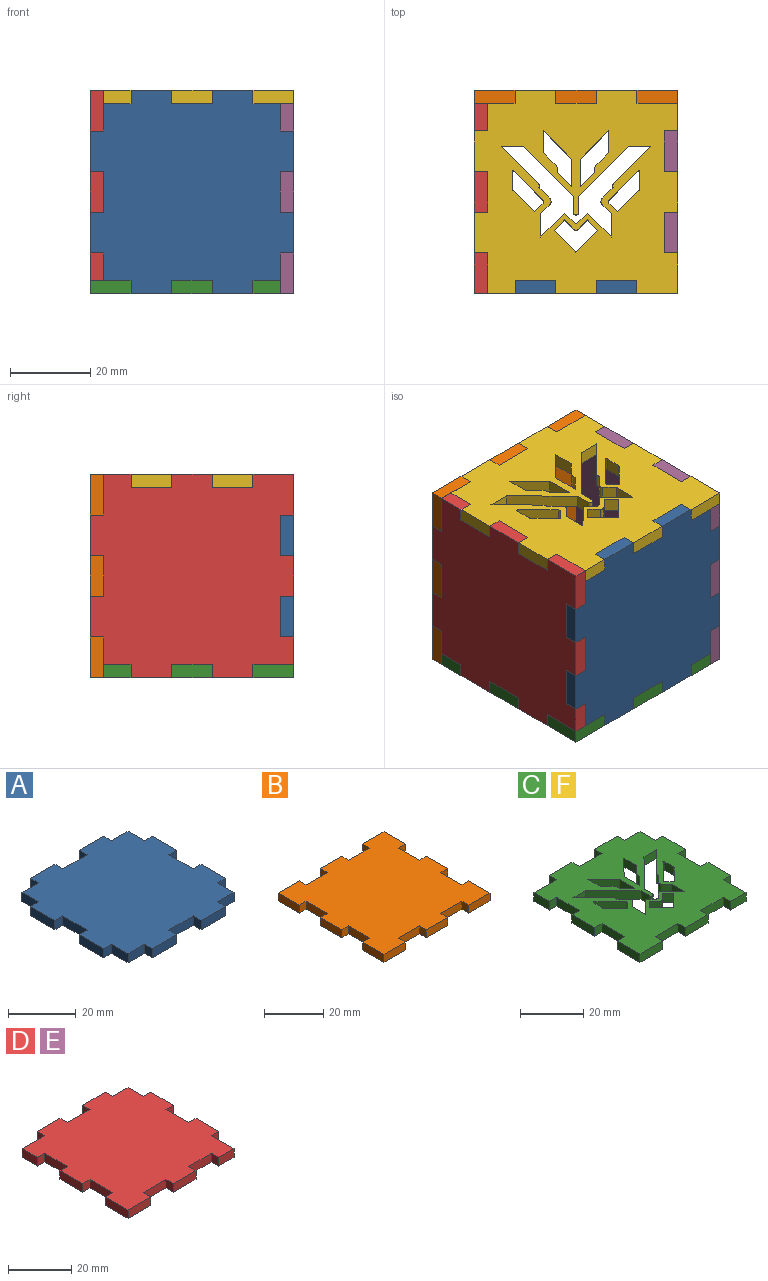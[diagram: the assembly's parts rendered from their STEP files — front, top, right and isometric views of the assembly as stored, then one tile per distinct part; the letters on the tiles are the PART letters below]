
ASSEMBLY  parts=6 mates=5
PART A: 38 faces, bbox 50.8x50.8x3.3 mm
  f0: plane 3.3x3.3mm, normal (-1,0,0), area 10.9mm2, adj f1,f35,f36,f37
  f1: plane 6.86x3.3mm, normal (0,1,0), area 22.6mm2, adj f0,f2,f36,f37
  f2: plane 6.86x3.3mm, normal (-1,0,0), area 22.6mm2, adj f1,f3,f36,f37
  f3: plane 3.3x3.3mm, normal (0,1,0), area 10.9mm2, adj f2,f4,f36,f37
  f4: plane 10.16x3.3mm, normal (-1,0,0), area 33.5mm2, adj f3,f5,f36,f37
  f5: plane 3.3x3.3mm, normal (0,-1,0), area 10.9mm2, adj f4,f6,f36,f37
  f6: plane 10.16x3.3mm, normal (-1,0,0), area 33.5mm2, adj f5,f7,f36,f37
  f7: plane 3.3x3.3mm, normal (0,1,0), area 10.9mm2, adj f6,f8,f36,f37
  f8: plane 10.16x3.3mm, normal (-1,0,0), area 33.5mm2, adj f7,f9,f36,f37
  f9: plane 3.3x3.3mm, normal (0,-1,0), area 10.9mm2, adj f8,f10,f36,f37
  f10: plane 6.86x3.3mm, normal (-1,0,0), area 22.6mm2, adj f9,f11,f36,f37
  f11: plane 6.86x3.3mm, normal (0,-1,0), area 22.6mm2, adj f10,f12,f36,f37
  f12: plane 3.3x3.3mm, normal (-1,0,0), area 10.9mm2, adj f11,f13,f36,f37
  f13: plane 10.16x3.3mm, normal (0,-1,0), area 33.5mm2, adj f12,f14,f36,f37
  f14: plane 3.3x3.3mm, normal (1,0,0), area 10.9mm2, adj f13,f15,f36,f37
  f15: plane 10.16x3.3mm, normal (0,-1,0), area 33.5mm2, adj f14,f16,f36,f37
  f16: plane 3.3x3.3mm, normal (-1,0,0), area 10.9mm2, adj f15,f17,f36,f37
  f17: plane 10.16x3.3mm, normal (0,-1,0), area 33.5mm2, adj f16,f18,f36,f37
  f18: plane 3.3x3.3mm, normal (1,0,0), area 10.9mm2, adj f17,f19,f36,f37
  f19: plane 6.86x3.3mm, normal (0,-1,0), area 22.6mm2, adj f18,f20,f36,f37
  f20: plane 6.86x3.3mm, normal (1,0,0), area 22.6mm2, adj f19,f21,f36,f37
  f21: plane 3.3x3.3mm, normal (0,-1,0), area 10.9mm2, adj f20,f22,f36,f37
  f22: plane 10.16x3.3mm, normal (1,0,0), area 33.5mm2, adj f21,f23,f36,f37
  f23: plane 3.3x3.3mm, normal (0,1,0), area 10.9mm2, adj f22,f24,f36,f37
  f24: plane 10.16x3.3mm, normal (1,0,0), area 33.5mm2, adj f23,f25,f36,f37
  f25: plane 3.3x3.3mm, normal (0,-1,0), area 10.9mm2, adj f24,f26,f36,f37
  f26: plane 10.16x3.3mm, normal (1,0,0), area 33.5mm2, adj f25,f27,f36,f37
  f27: plane 3.3x3.3mm, normal (0,1,0), area 10.9mm2, adj f26,f28,f36,f37
  f28: plane 6.86x3.3mm, normal (1,0,0), area 22.6mm2, adj f27,f29,f36,f37
  f29: plane 6.86x3.3mm, normal (0,1,0), area 22.6mm2, adj f28,f30,f36,f37
  f30: plane 3.3x3.3mm, normal (1,0,0), area 10.9mm2, adj f29,f31,f36,f37
  f31: plane 10.16x3.3mm, normal (0,1,0), area 33.5mm2, adj f30,f32,f36,f37
  f32: plane 3.3x3.3mm, normal (-1,0,0), area 10.9mm2, adj f31,f33,f36,f37
  f33: plane 10.16x3.3mm, normal (0,1,0), area 33.5mm2, adj f32,f34,f36,f37
  f34: plane 3.3x3.3mm, normal (1,0,0), area 10.9mm2, adj f33,f35,f36,f37
  f35: plane 10.16x3.3mm, normal (0,1,0), area 33.5mm2, adj f0,f34,f36,f37
  f36: plane 50.8x50.8mm, normal (0,0,1), area 2221.9mm2, adj f0,f1,f2,f3,f4,f5,f6,f7
  f37: plane 50.8x50.8mm, normal (0,0,-1), area 2221.9mm2, adj f0,f1,f2,f3,f4,f5,f6,f7
PART B: 38 faces, bbox 50.8x50.8x3.3 mm
  f0: plane 10.16x3.3mm, normal (0,1,0), area 33.5mm2, adj f1,f35,f36,f37
  f1: plane 10.16x3.3mm, normal (-1,0,0), area 33.5mm2, adj f0,f2,f36,f37
  f2: plane 3.3x3.3mm, normal (0,-1,0), area 10.9mm2, adj f1,f3,f36,f37
  f3: plane 10.16x3.3mm, normal (-1,0,0), area 33.5mm2, adj f2,f4,f36,f37
  f4: plane 3.3x3.3mm, normal (0,1,0), area 10.9mm2, adj f3,f5,f36,f37
  f5: plane 10.16x3.3mm, normal (-1,0,0), area 33.5mm2, adj f4,f6,f36,f37
  f6: plane 3.3x3.3mm, normal (0,-1,0), area 10.9mm2, adj f5,f7,f36,f37
  f7: plane 10.16x3.3mm, normal (-1,0,0), area 33.5mm2, adj f6,f8,f36,f37
  f8: plane 3.3x3.3mm, normal (0,1,0), area 10.9mm2, adj f7,f9,f36,f37
  f9: plane 10.16x3.3mm, normal (-1,0,0), area 33.5mm2, adj f8,f10,f36,f37
  f10: plane 10.16x3.3mm, normal (0,-1,0), area 33.5mm2, adj f9,f11,f36,f37
  f11: plane 3.3x3.3mm, normal (1,0,0), area 10.9mm2, adj f10,f12,f36,f37
  f12: plane 10.16x3.3mm, normal (0,-1,0), area 33.5mm2, adj f11,f13,f36,f37
  f13: plane 3.3x3.3mm, normal (-1,0,0), area 10.9mm2, adj f12,f14,f36,f37
  f14: plane 10.16x3.3mm, normal (0,-1,0), area 33.5mm2, adj f13,f15,f36,f37
  f15: plane 3.3x3.3mm, normal (1,0,0), area 10.9mm2, adj f14,f16,f36,f37
  f16: plane 10.16x3.3mm, normal (0,-1,0), area 33.5mm2, adj f15,f17,f36,f37
  f17: plane 3.3x3.3mm, normal (-1,0,0), area 10.9mm2, adj f16,f18,f36,f37
  f18: plane 10.16x3.3mm, normal (0,-1,0), area 33.5mm2, adj f17,f19,f36,f37
  f19: plane 10.16x3.3mm, normal (1,0,0), area 33.5mm2, adj f18,f20,f36,f37
  f20: plane 3.3x3.3mm, normal (0,1,0), area 10.9mm2, adj f19,f21,f36,f37
  f21: plane 10.16x3.3mm, normal (1,0,0), area 33.5mm2, adj f20,f22,f36,f37
  f22: plane 3.3x3.3mm, normal (0,-1,0), area 10.9mm2, adj f21,f23,f36,f37
  f23: plane 10.16x3.3mm, normal (1,0,0), area 33.5mm2, adj f22,f24,f36,f37
  f24: plane 3.3x3.3mm, normal (0,1,0), area 10.9mm2, adj f23,f25,f36,f37
  f25: plane 10.16x3.3mm, normal (1,0,0), area 33.5mm2, adj f24,f26,f36,f37
  f26: plane 3.3x3.3mm, normal (0,-1,0), area 10.9mm2, adj f25,f27,f36,f37
  f27: plane 10.16x3.3mm, normal (1,0,0), area 33.5mm2, adj f26,f28,f36,f37
  f28: plane 10.16x3.3mm, normal (0,1,0), area 33.5mm2, adj f27,f29,f36,f37
  f29: plane 3.3x3.3mm, normal (-1,0,0), area 10.9mm2, adj f28,f30,f36,f37
  f30: plane 10.16x3.3mm, normal (0,1,0), area 33.5mm2, adj f29,f31,f36,f37
  f31: plane 3.3x3.3mm, normal (1,0,0), area 10.9mm2, adj f30,f32,f36,f37
  f32: plane 10.16x3.3mm, normal (0,1,0), area 33.5mm2, adj f31,f33,f36,f37
  f33: plane 3.3x3.3mm, normal (-1,0,0), area 10.9mm2, adj f32,f34,f36,f37
  f34: plane 10.16x3.3mm, normal (0,1,0), area 33.5mm2, adj f33,f35,f36,f37
  f35: plane 3.3x3.3mm, normal (1,0,0), area 10.9mm2, adj f0,f34,f36,f37
  f36: plane 50.8x50.8mm, normal (0,0,1), area 2312.4mm2, adj f0,f1,f2,f3,f4,f5,f6,f7
  f37: plane 50.8x50.8mm, normal (0,0,-1), area 2312.4mm2, adj f0,f1,f2,f3,f4,f5,f6,f7
PART C: 98 faces, bbox 50.8x50.8x3.3 mm
  f0: extruded ~3.3x0.46mm, area 2.6mm2, adj f1,f95,f96,f97
  f1: plane 3.84x3.3mm, normal (-1,0,0), area 12.7mm2, adj f0,f2,f96,f97
  f2: extruded ~3.3x0.62mm, area 2.3mm2, adj f1,f3,f96,f97
  f3: plane 5.31x5.27mm, normal (-0.71,0.7,0), area 24.7mm2, adj f2,f4,f96,f97
  f4: plane 3.3x2.18mm, normal (0.71,0.7,0), area 10.1mm2, adj f3,f5,f96,f97
  f5: extruded ~3.3x0.8mm, area 2.9mm2, adj f4,f95,f96,f97
  f6: plane 12.55x12.45mm, normal (-0.71,-0.7,0), area 58.3mm2, adj f7,f89,f96,f97
  f7: plane 3.61x3.3mm, normal (-1,0,0), area 11.9mm2, adj f6,f8,f96,f97
  f8: extruded ~3.3x0.97mm, area 4.4mm2, adj f7,f9,f96,f97
  f9: extruded ~3.3x0.97mm, area 4.4mm2, adj f8,f10,f96,f97
  f10: plane 3.61x3.3mm, normal (1,0,0), area 11.9mm2, adj f9,f11,f96,f97
  f11: plane 12.55x12.45mm, normal (0.71,-0.7,0), area 58.3mm2, adj f10,f12,f96,f97
  f12: plane 5.5x3.3mm, normal (0,-1,0), area 18.2mm2, adj f11,f13,f96,f97
  f13: plane 9.17x9.09mm, normal (-0.71,0.7,0), area 42.6mm2, adj f12,f14,f96,f97
  f14: extruded ~3.3x1.15mm, area 4.4mm2, adj f13,f15,f96,f97
  f15: plane 3.3x2.62mm, normal (-0.71,0.7,0), area 12.2mm2, adj f14,f16,f96,f97
  f16: extruded ~3.3x1.47mm, area 5.4mm2, adj f15,f17,f96,f97
  f17: plane 3.3x2.36mm, normal (-0.7,-0.71,0), area 11mm2, adj f16,f18,f96,f97
  f18: plane 5.93x3.3mm, normal (-1,0,0), area 19.6mm2, adj f17,f19,f96,f97
  f19: plane 5.98x5.93mm, normal (0.7,0.71,0), area 27.8mm2, adj f18,f20,f96,f97
  f20: plane 3.3x2.18mm, normal (-0.71,0.7,0), area 10.1mm2, adj f19,f21,f96,f97
  f21: extruded ~3.3x0.7mm, area 2.5mm2, adj f20,f22,f96,f97
  f22: extruded ~3.3x0.7mm, area 2.5mm2, adj f21,f23,f96,f97
  f23: plane 3.3x2.18mm, normal (0.71,0.7,0), area 10.1mm2, adj f22,f24,f96,f97
  f24: plane 5.98x5.93mm, normal (-0.7,0.71,0), area 27.8mm2, adj f23,f25,f96,f97
  f25: plane 5.93x3.3mm, normal (1,0,0), area 19.6mm2, adj f24,f26,f96,f97
  f26: plane 3.3x2.36mm, normal (0.7,-0.71,0), area 11mm2, adj f25,f27,f96,f97
  f27: extruded ~3.3x1.47mm, area 5.4mm2, adj f26,f28,f96,f97
  f28: plane 3.3x2.62mm, normal (0.71,0.7,0), area 12.2mm2, adj f27,f29,f96,f97
  f29: extruded ~3.3x1.15mm, area 4.4mm2, adj f28,f30,f96,f97
  f30: plane 9.17x9.09mm, normal (0.71,0.7,0), area 42.6mm2, adj f29,f89,f96,f97
  f31: plane 3.3x2.58mm, normal (-0.7,-0.71,0), area 12mm2, adj f32,f90,f96,f97
  f32: plane 5.51x5.47mm, normal (-0.71,0.7,0), area 25.6mm2, adj f31,f33,f96,f97
  f33: plane 5.51x5.47mm, normal (0.71,0.7,0), area 25.6mm2, adj f32,f34,f96,f97
  f34: plane 3.3x2.58mm, normal (0.7,-0.71,0), area 12mm2, adj f33,f35,f96,f97
  f35: plane 3.3x2.26mm, normal (-0.71,-0.7,0), area 10.5mm2, adj f34,f36,f96,f97
  f36: extruded ~3.3x0.65mm, area 2.4mm2, adj f35,f37,f96,f97
  f37: extruded ~3.3x0.65mm, area 2.4mm2, adj f36,f90,f96,f97
  f38: plane 6.89x3.3mm, normal (1,0,0), area 22.7mm2, adj f39,f91,f96,f97
  f39: plane 7.14x7.08mm, normal (0.71,-0.7,0), area 33.2mm2, adj f38,f40,f96,f97
  f40: plane 5.57x3.3mm, normal (-1,0,0), area 18.4mm2, adj f39,f41,f96,f97
  f41: plane 3.3x2.9mm, normal (-0.71,0.7,0), area 13.5mm2, adj f40,f42,f96,f97
  f42: extruded ~3.3x2.03mm, area 7.3mm2, adj f41,f91,f96,f97
  f43: extruded ~3.3x0.46mm, area 2.6mm2, adj f44,f92,f96,f97
  f44: plane 7.2x7.14mm, normal (-0.71,-0.7,0), area 33.5mm2, adj f43,f45,f96,f97
  f45: extruded ~3.3x0.8mm, area 2.9mm2, adj f44,f46,f96,f97
  f46: plane 3.3x2.18mm, normal (-0.71,0.7,0), area 10.1mm2, adj f45,f47,f96,f97
  f47: plane 5.31x5.27mm, normal (0.71,0.7,0), area 24.7mm2, adj f46,f48,f96,f97
  f48: extruded ~3.3x0.62mm, area 2.3mm2, adj f47,f92,f96,f97
  f49: plane 7.14x7.08mm, normal (-0.71,-0.7,0), area 33.2mm2, adj f50,f93,f96,f97
  f50: plane 6.89x3.3mm, normal (-1,0,0), area 22.7mm2, adj f49,f51,f96,f97
  f51: plane 3.53x3.5mm, normal (0.71,0.7,0), area 16.4mm2, adj f50,f52,f96,f97
  f52: extruded ~3.3x2.03mm, area 7.3mm2, adj f51,f53,f96,f97
  f53: plane 3.3x2.9mm, normal (0.71,0.7,0), area 13.5mm2, adj f52,f93,f96,f97
  f54: plane 10.16x3.3mm, normal (1,0,0), area 33.5mm2, adj f55,f94,f96,f97
  f55: plane 3.3x3.3mm, normal (0,-1,0), area 10.9mm2, adj f54,f56,f96,f97
  f56: plane 10.16x3.3mm, normal (1,0,0), area 33.5mm2, adj f55,f57,f96,f97
  f57: plane 3.3x3.3mm, normal (0,1,0), area 10.9mm2, adj f56,f58,f96,f97
  f58: plane 10.16x3.3mm, normal (1,0,0), area 33.5mm2, adj f57,f59,f96,f97
  f59: plane 3.3x3.3mm, normal (0,-1,0), area 10.9mm2, adj f58,f60,f96,f97
  f60: plane 10.16x3.3mm, normal (1,0,0), area 33.5mm2, adj f59,f61,f96,f97
  f61: plane 3.3x3.3mm, normal (0,1,0), area 10.9mm2, adj f60,f62,f96,f97
  f62: plane 6.86x3.3mm, normal (1,0,0), area 22.6mm2, adj f61,f63,f96,f97
  f63: plane 6.86x3.3mm, normal (0,1,0), area 22.6mm2, adj f62,f64,f96,f97
  f64: plane 3.3x3.3mm, normal (1,0,0), area 10.9mm2, adj f63,f65,f96,f97
  f65: plane 10.16x3.3mm, normal (0,1,0), area 33.5mm2, adj f64,f66,f96,f97
  f66: plane 3.3x3.3mm, normal (-1,0,0), area 10.9mm2, adj f65,f67,f96,f97
  f67: plane 10.16x3.3mm, normal (0,1,0), area 33.5mm2, adj f66,f68,f96,f97
  f68: plane 3.3x3.3mm, normal (1,0,0), area 10.9mm2, adj f67,f69,f96,f97
  f69: plane 10.16x3.3mm, normal (0,1,0), area 33.5mm2, adj f68,f70,f96,f97
  f70: plane 3.3x3.3mm, normal (-1,0,0), area 10.9mm2, adj f69,f71,f96,f97
  f71: plane 10.16x3.3mm, normal (0,1,0), area 33.5mm2, adj f70,f72,f96,f97
  f72: plane 6.86x3.3mm, normal (-1,0,0), area 22.6mm2, adj f71,f73,f96,f97
  f73: plane 3.3x3.3mm, normal (0,-1,0), area 10.9mm2, adj f72,f74,f96,f97
  f74: plane 10.16x3.3mm, normal (-1,0,0), area 33.5mm2, adj f73,f75,f96,f97
  f75: plane 3.3x3.3mm, normal (0,1,0), area 10.9mm2, adj f74,f76,f96,f97
  f76: plane 10.16x3.3mm, normal (-1,0,0), area 33.5mm2, adj f75,f77,f96,f97
  f77: plane 3.3x3.3mm, normal (0,-1,0), area 10.9mm2, adj f76,f78,f96,f97
  f78: plane 10.16x3.3mm, normal (-1,0,0), area 33.5mm2, adj f77,f79,f96,f97
  f79: plane 3.3x3.3mm, normal (0,1,0), area 10.9mm2, adj f78,f80,f96,f97
  f80: plane 10.16x3.3mm, normal (-1,0,0), area 33.5mm2, adj f79,f81,f96,f97
  f81: plane 10.16x3.3mm, normal (0,-1,0), area 33.5mm2, adj f80,f82,f96,f97
  f82: plane 3.3x3.3mm, normal (1,0,0), area 10.9mm2, adj f81,f83,f96,f97
  f83: plane 10.16x3.3mm, normal (0,-1,0), area 33.5mm2, adj f82,f84,f96,f97
  f84: plane 3.3x3.3mm, normal (-1,0,0), area 10.9mm2, adj f83,f85,f96,f97
  f85: plane 10.16x3.3mm, normal (0,-1,0), area 33.5mm2, adj f84,f86,f96,f97
  f86: plane 3.3x3.3mm, normal (1,0,0), area 10.9mm2, adj f85,f87,f96,f97
  f87: plane 10.16x3.3mm, normal (0,-1,0), area 33.5mm2, adj f86,f88,f96,f97
  f88: plane 3.3x3.3mm, normal (-1,0,0), area 10.9mm2, adj f87,f94,f96,f97
  f89: plane 5.5x3.3mm, normal (0,-1,0), area 18.2mm2, adj f6,f30,f96,f97
  f90: plane 3.3x2.26mm, normal (0.71,-0.7,0), area 10.5mm2, adj f31,f37,f96,f97
  f91: plane 3.53x3.5mm, normal (-0.71,0.7,0), area 16.4mm2, adj f38,f42,f96,f97
  f92: plane 3.84x3.3mm, normal (1,0,0), area 12.7mm2, adj f43,f48,f96,f97
  f93: plane 5.57x3.3mm, normal (1,0,0), area 18.4mm2, adj f49,f53,f96,f97
  f94: plane 6.86x3.3mm, normal (0,-1,0), area 22.6mm2, adj f54,f88,f96,f97
  f95: plane 7.2x7.14mm, normal (0.71,-0.7,0), area 33.5mm2, adj f0,f5,f96,f97
  f96: plane 50.8x50.8mm, normal (0,0,1), area 1817.5mm2, adj f0,f1,f2,f3,f4,f5,f6,f7
  f97: plane 50.8x50.8mm, normal (0,0,-1), area 1817.5mm2, adj f0,f1,f2,f3,f4,f5,f6,f7
PART D: 38 faces, bbox 50.8x50.8x3.3 mm
  f0: plane 3.3x3.3mm, normal (1,0,0), area 10.9mm2, adj f1,f35,f36,f37
  f1: plane 10.16x3.3mm, normal (0,-1,0), area 33.5mm2, adj f0,f2,f36,f37
  f2: plane 3.3x3.3mm, normal (-1,0,0), area 10.9mm2, adj f1,f3,f36,f37
  f3: plane 10.16x3.3mm, normal (0,-1,0), area 33.5mm2, adj f2,f4,f36,f37
  f4: plane 3.3x3.3mm, normal (1,0,0), area 10.9mm2, adj f3,f5,f36,f37
  f5: plane 10.16x3.3mm, normal (0,-1,0), area 33.5mm2, adj f4,f6,f36,f37
  f6: plane 3.3x3.3mm, normal (-1,0,0), area 10.9mm2, adj f5,f7,f36,f37
  f7: plane 6.86x3.3mm, normal (0,-1,0), area 22.6mm2, adj f6,f8,f36,f37
  f8: plane 10.16x3.3mm, normal (1,0,0), area 33.5mm2, adj f7,f9,f36,f37
  f9: plane 3.3x3.3mm, normal (0,-1,0), area 10.9mm2, adj f8,f10,f36,f37
  f10: plane 10.16x3.3mm, normal (1,0,0), area 33.5mm2, adj f9,f11,f36,f37
  f11: plane 3.3x3.3mm, normal (0,1,0), area 10.9mm2, adj f10,f12,f36,f37
  f12: plane 10.16x3.3mm, normal (1,0,0), area 33.5mm2, adj f11,f13,f36,f37
  f13: plane 3.3x3.3mm, normal (0,-1,0), area 10.9mm2, adj f12,f14,f36,f37
  f14: plane 10.16x3.3mm, normal (1,0,0), area 33.5mm2, adj f13,f15,f36,f37
  f15: plane 3.3x3.3mm, normal (0,1,0), area 10.9mm2, adj f14,f16,f36,f37
  f16: plane 6.86x3.3mm, normal (1,0,0), area 22.6mm2, adj f15,f17,f36,f37
  f17: plane 6.86x3.3mm, normal (0,1,0), area 22.6mm2, adj f16,f18,f36,f37
  f18: plane 3.3x3.3mm, normal (1,0,0), area 10.9mm2, adj f17,f19,f36,f37
  f19: plane 10.16x3.3mm, normal (0,1,0), area 33.5mm2, adj f18,f20,f36,f37
  f20: plane 3.3x3.3mm, normal (-1,0,0), area 10.9mm2, adj f19,f21,f36,f37
  f21: plane 10.16x3.3mm, normal (0,1,0), area 33.5mm2, adj f20,f22,f36,f37
  f22: plane 3.3x3.3mm, normal (1,0,0), area 10.9mm2, adj f21,f23,f36,f37
  f23: plane 10.16x3.3mm, normal (0,1,0), area 33.5mm2, adj f22,f24,f36,f37
  f24: plane 3.3x3.3mm, normal (-1,0,0), area 10.9mm2, adj f23,f25,f36,f37
  f25: plane 10.16x3.3mm, normal (0,1,0), area 33.5mm2, adj f24,f26,f36,f37
  f26: plane 6.86x3.3mm, normal (-1,0,0), area 22.6mm2, adj f25,f27,f36,f37
  f27: plane 3.3x3.3mm, normal (0,-1,0), area 10.9mm2, adj f26,f28,f36,f37
  f28: plane 10.16x3.3mm, normal (-1,0,0), area 33.5mm2, adj f27,f29,f36,f37
  f29: plane 3.3x3.3mm, normal (0,1,0), area 10.9mm2, adj f28,f30,f36,f37
  f30: plane 10.16x3.3mm, normal (-1,0,0), area 33.5mm2, adj f29,f31,f36,f37
  f31: plane 3.3x3.3mm, normal (0,-1,0), area 10.9mm2, adj f30,f32,f36,f37
  f32: plane 10.16x3.3mm, normal (-1,0,0), area 33.5mm2, adj f31,f33,f36,f37
  f33: plane 3.3x3.3mm, normal (0,1,0), area 10.9mm2, adj f32,f34,f36,f37
  f34: plane 10.16x3.3mm, normal (-1,0,0), area 33.5mm2, adj f33,f35,f36,f37
  f35: plane 10.16x3.3mm, normal (0,-1,0), area 33.5mm2, adj f0,f34,f36,f37
  f36: plane 50.8x50.8mm, normal (0,0,1), area 2256.2mm2, adj f0,f1,f2,f3,f4,f5,f6,f7
  f37: plane 50.8x50.8mm, normal (0,0,-1), area 2256.2mm2, adj f0,f1,f2,f3,f4,f5,f6,f7
PART E: same geometry as D
PART F: same geometry as C
PLACE A rot(axis=(1,0,0),90deg) t=(-7.36,6.25,-46.96)mm
PLACE B rot(axis=(1,0,0),90deg) t=(-7.36,53.75,-46.96)mm
PLACE C t=(-7.36,53.75,-46.96)mm
PLACE D rot(axis=(0,1,0),90deg) t=(-7.36,53.75,3.84)mm
PLACE E rot(axis=(0,-1,0),90deg) t=(43.44,53.75,-46.96)mm
PLACE F rot(axis=(0,-1,0),180deg) t=(43.44,53.75,3.84)mm
MATE slider F.f73 <-> E.f15  axis (0,-1,0) through (41.79,43.59,2.19)mm
MATE slider D.f27 <-> F.f61  axis (0,-1,0) through (-5.71,43.59,2.19)mm
MATE slider A.f14 <-> C.f84  axis (1,0,0) through (12.96,4.6,-45.31)mm
MATE slider B.f2 <-> D.f24  axis (0,0,-1) through (-5.71,52.1,-6.32)mm
MATE slider C.f61 <-> E.f27  axis (0,1,0) through (41.79,43.59,-45.31)mm
